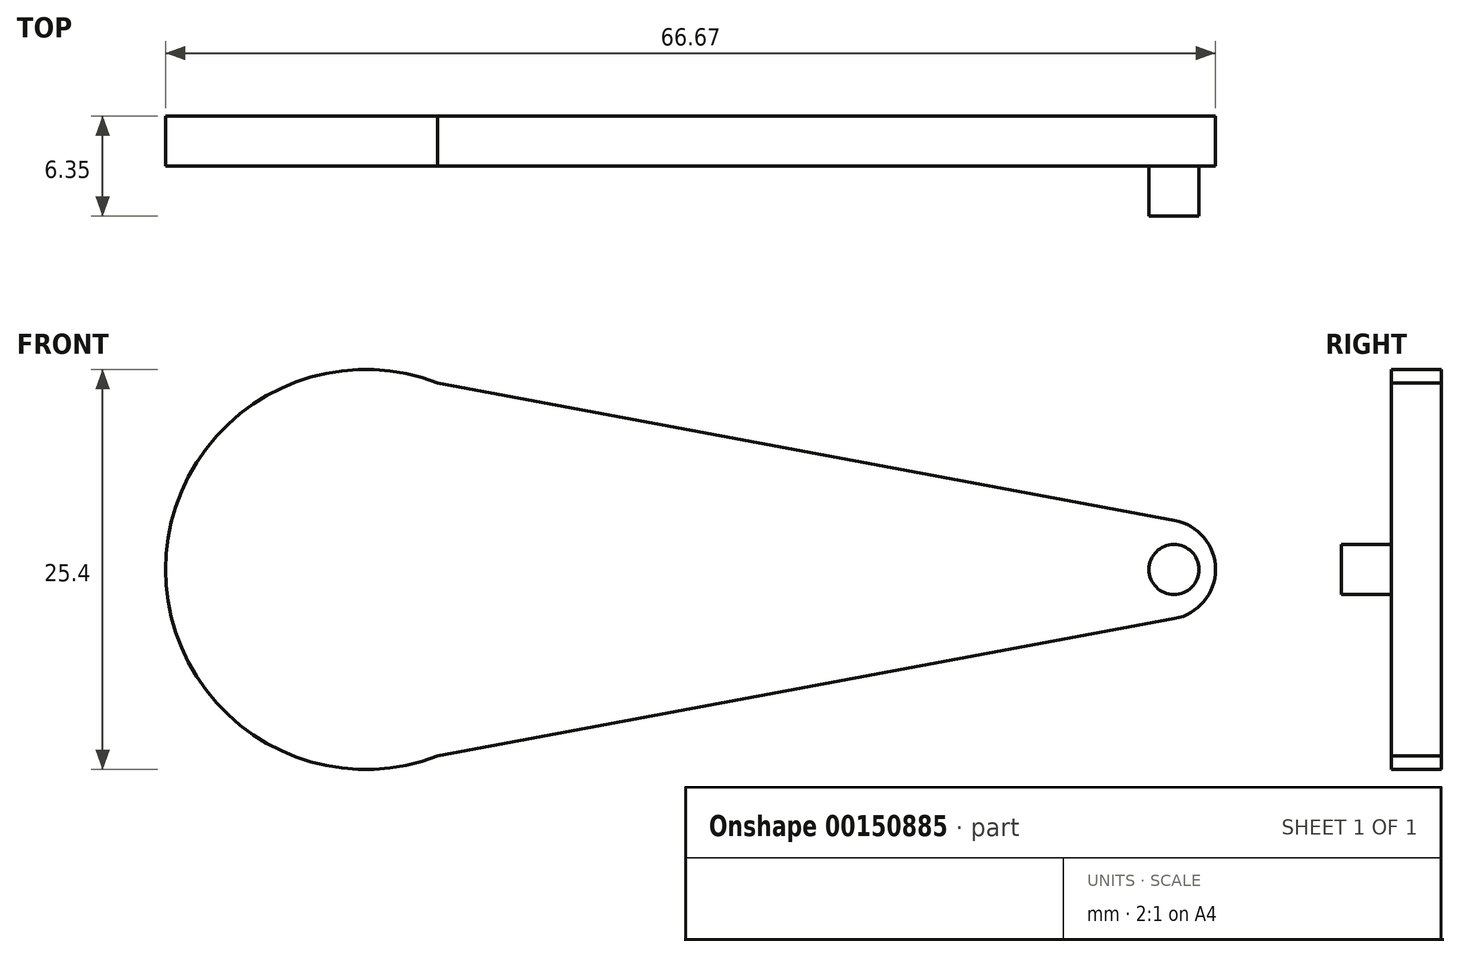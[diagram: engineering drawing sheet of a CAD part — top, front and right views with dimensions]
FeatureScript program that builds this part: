
annotation { "Feature Type Name" : "Feature", "Feature Type Description" : "" }
export const myFeature = defineFeature(function(context is Context, id is Id, definition is map)
    precondition{}
    {
        {
            var Q0;
            Q0=qCreatedBy(makeId("Front.planeOp"),FACE);
            var sketch = newSketch(context, id + "F0", { "sketchPlane" : qUnion([Q0])});
            skArc(sketch, "E0", {"start": v(4.58, 11.85) * mm, "mid": v(-12.7, 0) * mm, "end": v(4.58, -11.85) * mm});
            skArc(sketch, "E1", {"start": v(51.38, -3.12) * mm, "mid": v(53.98, 0) * mm, "end": v(51.38, 3.12) * mm});
            skLineSegment(sketch, "E2", {"start": v(0, 12.7) * mm, "end": v(51.38, 3.12) * mm});
            skLineSegment(sketch, "E3", {"start": v(0, -12.7) * mm, "end": v(51.38, -3.12) * mm});
            skSolve(sketch);
        }
        {
            var Q0;
            Q0 = qSketchRegion(id + "F0", true);
            extrude(context, id + "F1", {"entities" : qUnion([Q0]), "depth" : 3.17 * mm});
        }
        {
            var Q0;
            Q0=makeQuery(id+"F1.opExtrude","CAP_FACE",FACE,{"disambiguationData":[OSD([sQuery(id+"F0.wireOp",EDGE,"E0"),sQuery(id+"F0.wireOp",EDGE,"E1"),sQuery(id+"F0.wireOp",EDGE,"E2"),sQuery(id+"F0.wireOp",EDGE,"E3")])],"isStart":false});
            var sketch = newSketch(context, id + "F2", { "sketchPlane" : qUnion([Q0])});
            skCircle(sketch, "E4", {"center": v(51.34, 0) * mm, "radius": 1.59 * mm});
            skSolve(sketch);
        }
        {
            var Q0;
            Q0 = qSketchRegion(id + "F2", true);
            extrude(context, id + "F3", {"entities" : qUnion([Q0]), "operationType" : NewBodyOperationType.ADD, "depth" : 3.17 * mm});
        }
    });
